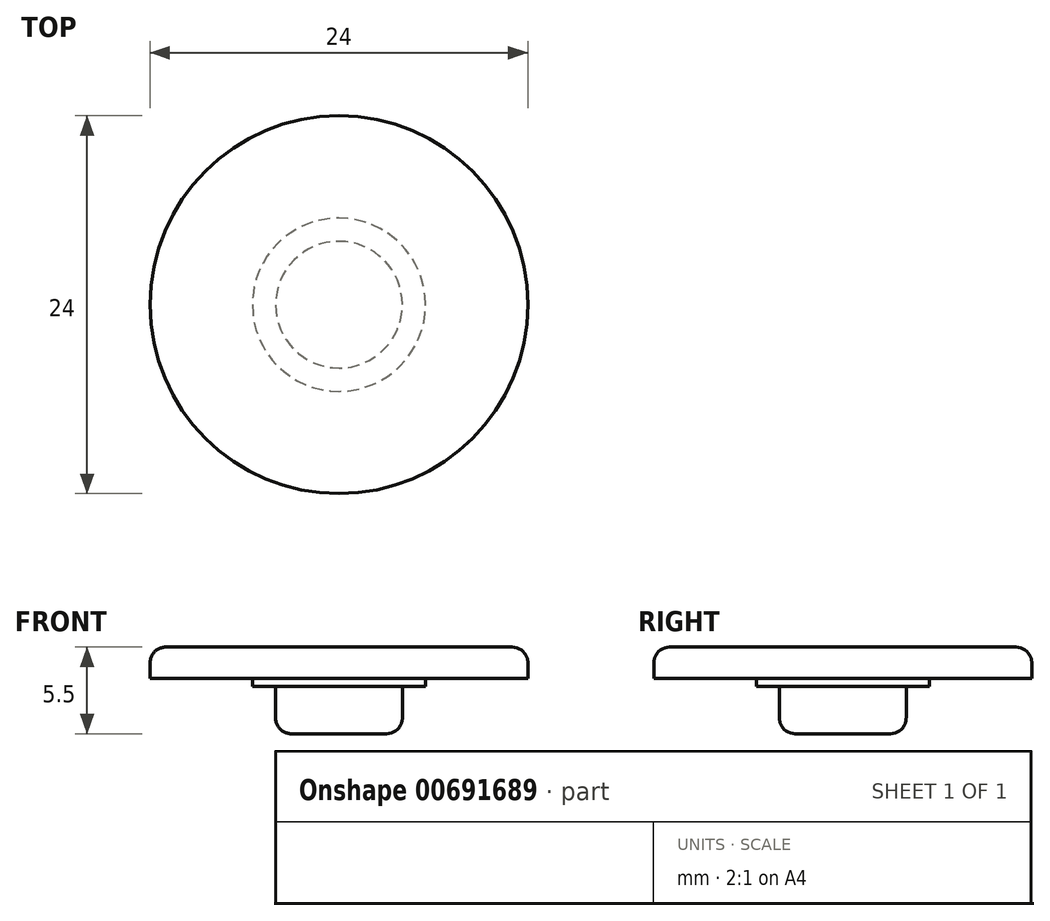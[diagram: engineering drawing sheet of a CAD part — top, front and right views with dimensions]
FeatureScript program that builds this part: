
annotation { "Feature Type Name" : "Feature", "Feature Type Description" : "" }
export const myFeature = defineFeature(function(context is Context, id is Id, definition is map)
    precondition{}
    {
        {
            var Q0;
            Q0=qCreatedBy(makeId("Front.planeOp"),FACE);
            var sketch = newSketch(context, id + "F0", { "sketchPlane" : qUnion([Q0])});
            skLineSegment(sketch, "E0", {"start": v(0, 0) * mm, "end": v(12, 0) * mm});
            skLineSegment(sketch, "E1", {"start": v(12, 0) * mm, "end": v(12, 2) * mm});
            skLineSegment(sketch, "E2", {"start": v(0, 0) * mm, "end": v(0, 2) * mm});
            skLineSegment(sketch, "E3", {"start": v(0, 2) * mm, "end": v(12, 2) * mm});
            skSolve(sketch);
        }
        {
            var Q0;
            Q0 = qSketchRegion(id + "F0", true);
            var Q1;
            Q1=sQuery(id+"F0.wireOp",EDGE,"E2");
            revolve(context, id + "F1", {"entities" : qUnion([Q0]), "axis" : qUnion([Q1]), "revolveType" : RevolveType.FULL});
        }
        {
            var Q0;
            Q0=makeQuery(id+"F1.opRevolve","SWEPT_EDGE",EDGE,{"disambiguationData":[OSD([sQuery(id+"F0.wireOp",EDGE,"E1"),sQuery(id+"F0.wireOp",EDGE,"E3")])]});
            fillet(context, id + "F2", {"entities" : qUnion([Q0]), "radius" : 1 * mm, "tangentPropagation" : true, "allowEdgeOverflow" : false});
        }
        {
            var Q0;
            Q0=makeQuery(id+"F1.opRevolve","SWEPT_FACE",FACE,{"disambiguationData":[OSD([sQuery(id+"F0.wireOp",EDGE,"E0")])]});
            var sketch = newSketch(context, id + "F3", { "sketchPlane" : qUnion([Q0])});
            skCircle(sketch, "E4", {"center": v(0, 0) * mm, "radius": 5.5 * mm});
            skSolve(sketch);
        }
        {
            var Q0;
            Q0 = qSketchRegion(id + "F3", true);
            extrude(context, id + "F4", {"entities" : qUnion([Q0]), "operationType" : NewBodyOperationType.ADD, "depth" : 0.5 * mm, "offsetDistance" : 25 * mm});
        }
        {
            var Q0;
            Q0=makeQuery(id+"F4.opExtrude","CAP_FACE",FACE,{"disambiguationData":[OSD([sQuery(id+"F3.wireOp",EDGE,"E4")])],"isStart":false});
            var sketch = newSketch(context, id + "F5", { "sketchPlane" : qUnion([Q0])});
            skCircle(sketch, "E5", {"center": v(0, 0) * mm, "radius": 4.03 * mm});
            skSolve(sketch);
        }
        {
            var Q0;
            Q0 = qSketchRegion(id + "F5", true);
            extrude(context, id + "F6", {"entities" : qUnion([Q0]), "operationType" : NewBodyOperationType.ADD, "depth" : 3 * mm, "offsetDistance" : 25 * mm});
        }
        {
            var Q0;
            Q0=makeQuery(id+"F6.opExtrude","CAP_EDGE",EDGE,{"disambiguationData":[OSD([sQuery(id+"F5.wireOp",EDGE,"E5")])],"isStart":false});
            fillet(context, id + "F7", {"entities" : qUnion([Q0]), "radius" : 1 * mm, "tangentPropagation" : true, "allowEdgeOverflow" : false});
        }
    });
